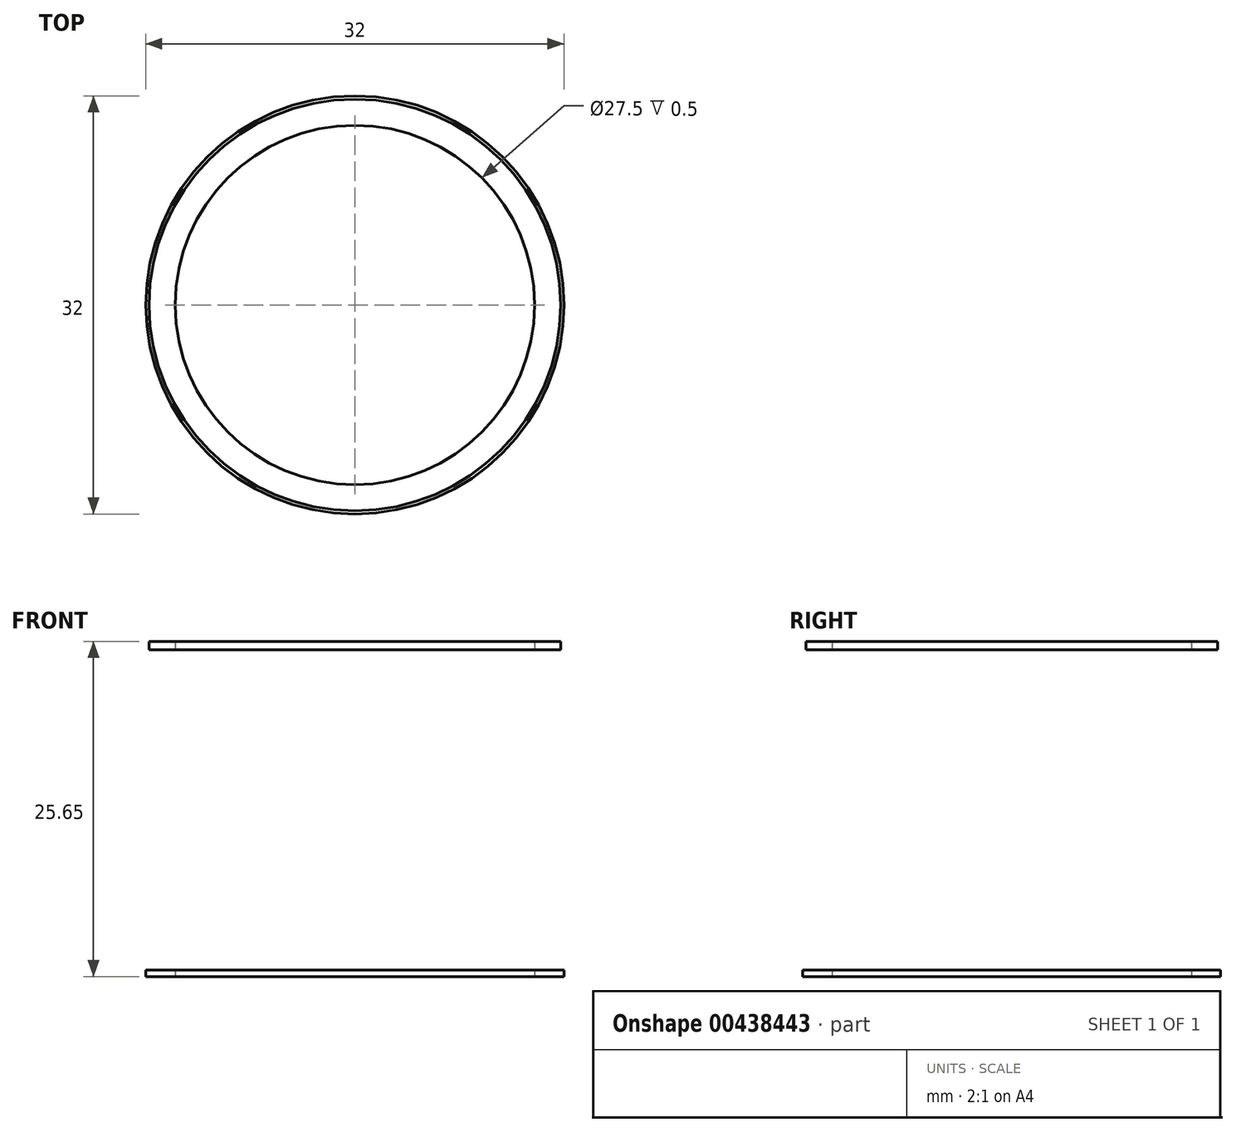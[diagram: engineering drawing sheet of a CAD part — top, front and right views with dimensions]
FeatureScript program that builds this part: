
annotation { "Feature Type Name" : "Feature", "Feature Type Description" : "" }
export const myFeature = defineFeature(function(context is Context, id is Id, definition is map)
    precondition{}
    {
        {
            var Q0;
            Q0=qCreatedBy(makeId("Top.planeOp"),FACE);
            var sketch = newSketch(context, id + "F0", { "sketchPlane" : qUnion([Q0])});
            skCircle(sketch, "E0", {"center": v(0, 0) * mm, "radius": 16 * mm});
            skCircle(sketch, "E1", {"center": v(0, 0) * mm, "radius": 13.75 * mm});
            skSolve(sketch);
        }
        {
            var Q0;
            Q0=makeQuery(id+"F0.imprint","IMPRINT",FACE,{"disambiguationData":[TD([[makeQuery(id+"F0.imprint","IMPRINT",EDGE,{"derivedFrom":sQuery(id+"F0.wireOp",EDGE,"E0")}),1.0]])]});
            extrude(context, id + "F1", {"entities" : qUnion([Q0]), "depth" : .5 * mm});
        }
        {
            var Q0;
            Q0=qCreatedBy(makeId("Top.planeOp"),FACE);
            cPlane(context, id + "F2", {"entities" : qUnion([Q0]), "cplaneType" : CPlaneType.OFFSET, "offset" : 25 * mm, "width" : 150 * mm, "height" : 150 * mm});
        }
        {
            var Q0;
            Q0=qCreatedBy(id+"F2.planeOp",FACE);
            var sketch = newSketch(context, id + "F3", { "sketchPlane" : qUnion([Q0])});
            skCircle(sketch, "E2", {"center": v(0, 0) * mm, "radius": 15.75 * mm});
            skCircle(sketch, "E3", {"center": v(0, 0) * mm, "radius": 13.75 * mm});
            skSolve(sketch);
        }
        {
            var Q0;
            Q0=makeQuery(id+"F3.imprint","IMPRINT",FACE,{"disambiguationData":[TD([[makeQuery(id+"F3.imprint","IMPRINT",EDGE,{"derivedFrom":sQuery(id+"F3.wireOp",EDGE,"E2")}),1.0]])]});
            extrude(context, id + "F4", {"entities" : qUnion([Q0]), "depth" : .65 * mm});
        }
    });
